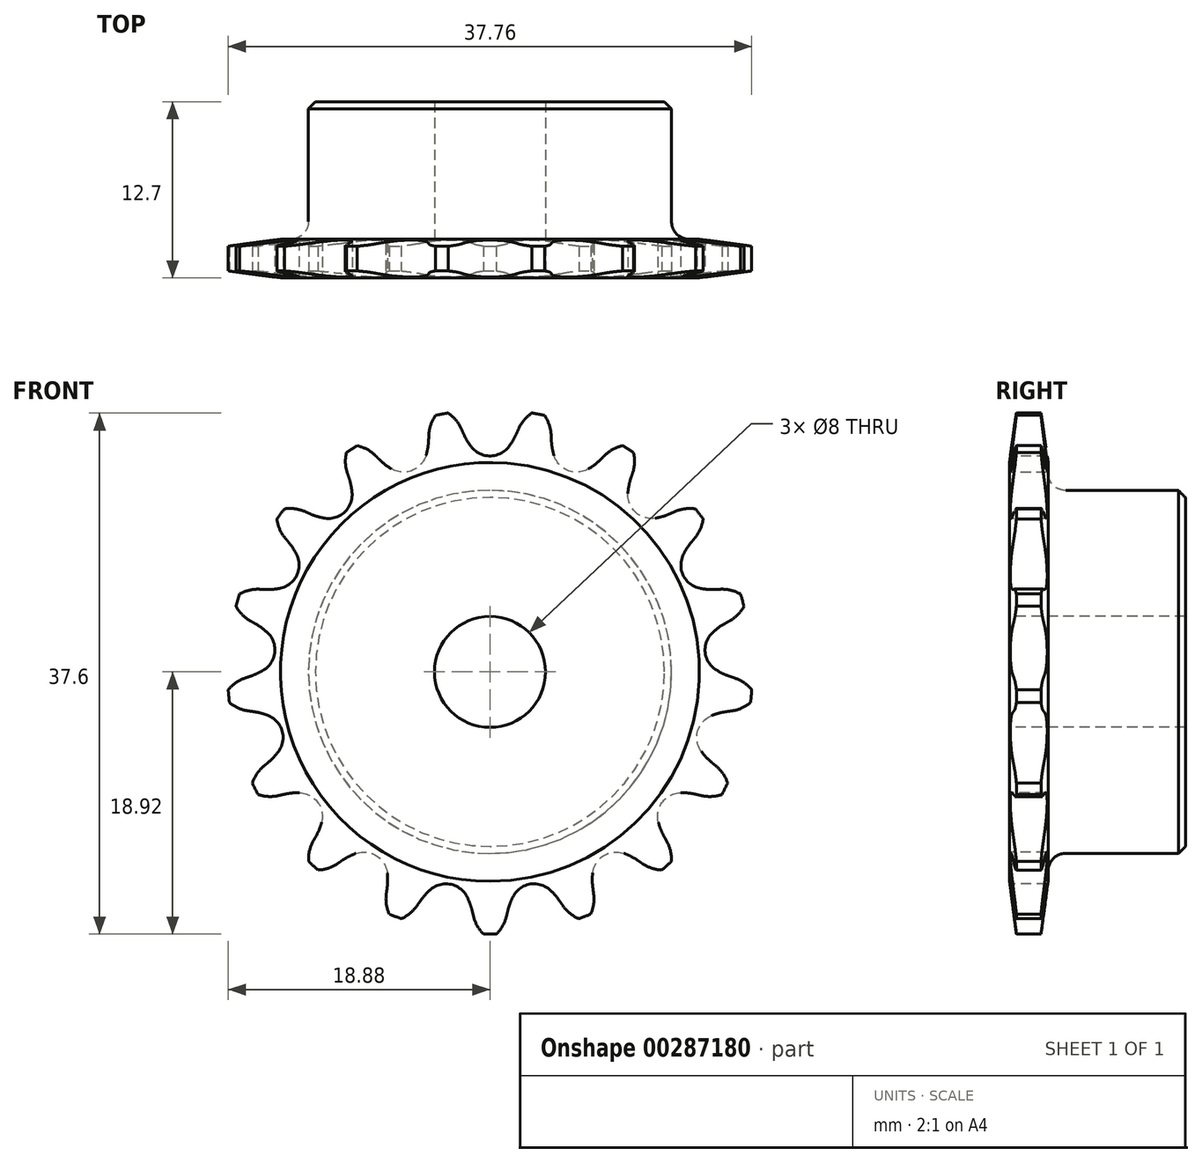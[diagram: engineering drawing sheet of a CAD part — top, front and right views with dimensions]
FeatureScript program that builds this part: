
annotation { "Feature Type Name" : "Feature", "Feature Type Description" : "" }
export const myFeature = defineFeature(function(context is Context, id is Id, definition is map)
    precondition{}
    {
        {
            var Q0;
            Q0=qCreatedBy(makeId("Right.planeOp"),FACE);
            var sketch = newSketch(context, id + "F0", { "sketchPlane" : qUnion([Q0])});
            skLineSegment(sketch, "E0", {"start": v(0, 0) * mm, "end": v(23.93, 0) * mm, "construction": true});
            skLineSegment(sketch, "E1.bottom", {"start": v(1.33, 13.1) * mm, "end": v(14.03, 13.1) * mm});
            skLineSegment(sketch, "E1.top", {"start": v(1.33, 4) * mm, "end": v(14.03, 4) * mm});
            skLineSegment(sketch, "E1.left", {"start": v(1.33, 13.1) * mm, "end": v(1.33, 4) * mm});
            skLineSegment(sketch, "E1.right", {"start": v(14.03, 13.1) * mm, "end": v(14.03, 4) * mm});
            skLineSegment(sketch, "E2.bottom", {"start": v(1.33, 4) * mm, "end": v(4.12, 4) * mm});
            skLineSegment(sketch, "E2.top", {"start": v(1.33, 18.92) * mm, "end": v(4.12, 18.92) * mm});
            skLineSegment(sketch, "E2.left", {"start": v(1.33, 4) * mm, "end": v(1.33, 18.92) * mm});
            skLineSegment(sketch, "E2.right", {"start": v(4.12, 4) * mm, "end": v(4.12, 18.92) * mm});
            skLineSegment(sketch, "E3.MirrorCS", {"start": v(1.33, -13.1) * mm, "end": v(1.33, -4) * mm});
            skLineSegment(sketch, "E4.MirrorCS", {"start": v(4.12, -4) * mm, "end": v(4.12, -18.92) * mm});
            skLineSegment(sketch, "E5.MirrorCS", {"start": v(1.33, -4) * mm, "end": v(1.33, -18.92) * mm});
            skLineSegment(sketch, "E6.MirrorCS", {"start": v(1.33, -13.1) * mm, "end": v(14.03, -13.1) * mm});
            skLineSegment(sketch, "E7.MirrorCS", {"start": v(1.33, -4) * mm, "end": v(14.03, -4) * mm});
            skLineSegment(sketch, "E8.MirrorCS", {"start": v(14.03, -13.1) * mm, "end": v(14.03, -4) * mm});
            skLineSegment(sketch, "E9.MirrorCS", {"start": v(1.33, -4) * mm, "end": v(4.12, -4) * mm});
            skLineSegment(sketch, "E10.MirrorCS", {"start": v(1.33, -18.92) * mm, "end": v(4.12, -18.92) * mm});
            skSolve(sketch);
        }
        {
            var Q0;
            {var subQ5=sQuery(id+"F0.wireOp",EDGE,"E2.top");Q0=makeQuery(id+"F0.imprint","IMPRINT",FACE,{"disambiguationData":[TD([[makeQuery(id+"F0.imprint","IMPRINT",EDGE,{"derivedFrom":subQ5}),-1.0]])]});}
            var Q1;
            {var subQ4=sQuery(id+"F0.wireOp",EDGE,"E1.top");Q1=makeQuery(id+"F0.imprint","IMPRINT",FACE,{"disambiguationData":[TD([[makeQuery(id+"F0.imprint","IMPRINT",EDGE,{"derivedFrom":subQ4}),1.0]])]});}
            var Q2;
            {var subQ0=sQuery(id+"F0.wireOp",EDGE,"E7.MirrorCS");Q2=makeQuery(id+"F0.imprint","IMPRINT",FACE,{"disambiguationData":[TD([[makeQuery(id+"F0.imprint","IMPRINT",EDGE,{"derivedFrom":subQ0}),-1.0]])]});}
            var Q3;
            {var subQ0=sQuery(id+"F0.wireOp",EDGE,"E10.MirrorCS");Q3=makeQuery(id+"F0.imprint","IMPRINT",FACE,{"disambiguationData":[TD([[makeQuery(id+"F0.imprint","IMPRINT",EDGE,{"derivedFrom":subQ0}),1.0]])]});}
            var Q4;
            {var subQ5=sQuery(id+"F0.wireOp",EDGE,"E2.bottom");Q4=makeQuery(id+"F0.imprint","IMPRINT",FACE,{"disambiguationData":[TD([[makeQuery(id+"F0.imprint","IMPRINT",EDGE,{"derivedFrom":subQ5}),1.0]])]});}
            var Q5;
            {var subQ0=sQuery(id+"F0.wireOp",EDGE,"E9.MirrorCS");Q5=makeQuery(id+"F0.imprint","IMPRINT",FACE,{"disambiguationData":[TD([[makeQuery(id+"F0.imprint","IMPRINT",EDGE,{"derivedFrom":subQ0}),-1.0]])]});}
            var Q6;
            Q6=sQuery(id+"F0.wireOp",EDGE,"E0");
            revolve(context, id + "F1", {"entities" : qUnion([Q0, Q1, Q2, Q3, Q4, Q5]), "axis" : qUnion([Q6]), "revolveType" : RevolveType.FULL});
        }
        {
            var Q0;
            Q0=makeQuery(id+"F1.opRevolve","SWEPT_EDGE",EDGE,{"disambiguationData":[OSD([sQuery(id+"F0.wireOp",EDGE,"E1.bottom"),sQuery(id+"F0.wireOp",EDGE,"E2.right")])]});
            fillet(context, id + "F2", {"entities" : qUnion([Q0]), "radius" : 1.27 * mm, "tangentPropagation" : true, "allowEdgeOverflow" : false});
        }
        {
            var Q0;
            Q0=makeQuery(id+"F1.opRevolve","SWEPT_BODY",BODY,{"disambiguationData":[OSD([sQuery(id+"F0.wireOp",EDGE,"E4.MirrorCS"),sQuery(id+"F0.wireOp",EDGE,"E5.MirrorCS"),sQuery(id+"F0.wireOp",EDGE,"E6.MirrorCS"),sQuery(id+"F0.wireOp",EDGE,"E7.MirrorCS"),sQuery(id+"F0.wireOp",EDGE,"E8.MirrorCS"),sQuery(id+"F0.wireOp",EDGE,"E9.MirrorCS"),sQuery(id+"F0.wireOp",EDGE,"E10.MirrorCS")])]});
            deleteBodies(context, id + "F3", {"entities" : qUnion([Q0])});
        }
        {
            var Q0;
            Q0=makeQuery(id+"F1.opRevolve","SWEPT_EDGE",EDGE,{"disambiguationData":[OSD([sQuery(id+"F0.wireOp",EDGE,"E1.bottom"),sQuery(id+"F0.wireOp",EDGE,"E1.right")])]});
            chamfer(context, id + "F4", {"entities" : qUnion([Q0]), "width" : 0.5 * mm, "tangentPropagation" : true});
        }
        {
            var Q0;
            Q0=makeQuery(id+"F1.opRevolve","SWEPT_EDGE",EDGE,{"disambiguationData":[OSD([sQuery(id+"F0.wireOp",EDGE,"E2.top"),sQuery(id+"F0.wireOp",EDGE,"E2.left")])]});
            var Q1;
            Q1=makeQuery(id+"F1.opRevolve","SWEPT_EDGE",EDGE,{"disambiguationData":[OSD([sQuery(id+"F0.wireOp",EDGE,"E2.top"),sQuery(id+"F0.wireOp",EDGE,"E2.right")])]});
            chamfer(context, id + "F5", {"entities" : qUnion([Q0, Q1]), "chamferType" : ChamferType.TWO_OFFSETS, "width1" : 3.8 * mm, "oppositeDirection" : false, "width2" : 0.5 * mm, "tangentPropagation" : true});
        }
        {
            var Q0;
            Q0=qCreatedBy(makeId("Front.planeOp"),FACE);
            var sketch = newSketch(context, id + "F6", { "sketchPlane" : qUnion([Q0])});
            skCircle(sketch, "E11", {"center": v(0, 0) * mm, "radius": 17.28 * mm, "construction": true});
            skLineSegment(sketch, "E12", {"start": v(0, 0) * mm, "end": v(0, 17.28) * mm, "construction": true});
            skLineSegment(sketch, "E13", {"start": v(0, 17.28) * mm, "end": v(75.89, 17.28) * mm, "construction": true});
            skLineSegment(sketch, "E14", {"start": v(0, 17.28) * mm, "end": v(2.07, 18.92) * mm, "construction": true});
            skLineSegment(sketch, "E15", {"start": v(2.07, 18.92) * mm, "end": v(-1.9, 17.17) * mm, "construction": true});
            skLineSegment(sketch, "E16", {"start": v(-1.9, 17.17) * mm, "end": v(-2.06, 17.53) * mm});
            skLineSegment(sketch, "E17", {"start": v(0, 0) * mm, "end": v(-3.54, 18.95) * mm, "construction": true});
            skArc(sketch, "E18", {"start": v(-3.54, 18.95) * mm, "mid": v(-6.56, 14.6) * mm, "end": v(-1.93, 17.17) * mm, "construction": true});
            skArc(sketch, "E19", {"start": v(-2.06, 17.53) * mm, "mid": v(-2.66, 18.39) * mm, "end": v(-3.54, 18.95) * mm});
            skArc(sketch, "E20", {"start": v(-1.9, 17.17) * mm, "mid": v(-1.65, 16.68) * mm, "end": v(-1.33, 16.22) * mm});
            skArc(sketch, "E21", {"start": v(-1.33, 16.22) * mm, "mid": v(2.68, 14.63) * mm, "end": v(6.08, 17.28) * mm, "construction": true});
            skArc(sketch, "E22.0.MirrorCS", {"start": v(1.9, 17.17) * mm, "mid": v(1.65, 16.68) * mm, "end": v(1.33, 16.22) * mm});
            skLineSegment(sketch, "E23.0.MirrorCS", {"start": v(1.9, 17.17) * mm, "end": v(2.06, 17.53) * mm});
            skArc(sketch, "E24.0.MirrorCS", {"start": v(2.06, 17.53) * mm, "mid": v(2.66, 18.39) * mm, "end": v(3.54, 18.95) * mm});
            skArc(sketch, "E25", {"start": v(-1.33, 16.22) * mm, "mid": v(0, 15.58) * mm, "end": v(1.33, 16.22) * mm});
            skArc(sketch, "E26", {"start": v(1.33, 16.22) * mm, "mid": v(0, 18.98) * mm, "end": v(-1.33, 16.22) * mm, "construction": true});
            skArc(sketch, "E27.trimOffspring", {"start": v(-1.9, 17.17) * mm, "mid": v(-1.9, 17.17) * mm, "end": v(-1.9, 17.17) * mm, "construction": true});
            skLineSegment(sketch, "E28.trimOffspring", {"start": v(3.1, 5.82) * mm, "end": v(0, 12.86) * mm, "construction": true});
            skLineSegment(sketch, "E29.1.0", {"start": v(-7.98, 15.32) * mm, "end": v(-8.25, 15.6) * mm});
            skArc(sketch, "E29.1.1", {"start": v(-8.25, 15.6) * mm, "mid": v(-9.12, 16.18) * mm, "end": v(-10.15, 16.4) * mm});
            skArc(sketch, "E29.1.2", {"start": v(-7.98, 15.32) * mm, "mid": v(-7.56, 14.96) * mm, "end": v(-7.1, 14.65) * mm});
            skArc(sketch, "E29.1.3", {"start": v(-7.1, 14.65) * mm, "mid": v(-5.63, 14.53) * mm, "end": v(-4.62, 15.6) * mm});
            skArc(sketch, "E29.1.4", {"start": v(-4.43, 16.7) * mm, "mid": v(-4.49, 16.15) * mm, "end": v(-4.62, 15.6) * mm});
            skLineSegment(sketch, "E29.1.5", {"start": v(-4.43, 16.7) * mm, "end": v(-4.41, 17.09) * mm});
            skArc(sketch, "E29.1.6", {"start": v(-4.41, 17.09) * mm, "mid": v(-4.16, 18.1) * mm, "end": v(-3.54, 18.95) * mm});
            skLineSegment(sketch, "E29.2.0", {"start": v(-12.97, 11.4) * mm, "end": v(-13.33, 11.56) * mm});
            skArc(sketch, "E29.2.1", {"start": v(-13.33, 11.56) * mm, "mid": v(-14.35, 11.8) * mm, "end": v(-15.39, 11.62) * mm});
            skArc(sketch, "E29.2.2", {"start": v(-12.97, 11.4) * mm, "mid": v(-12.45, 11.22) * mm, "end": v(-11.9, 11.1) * mm});
            skArc(sketch, "E29.2.3", {"start": v(-11.9, 11.1) * mm, "mid": v(-10.5, 11.51) * mm, "end": v(-9.95, 12.88) * mm});
            skArc(sketch, "E29.2.4", {"start": v(-10.16, 13.97) * mm, "mid": v(-10.02, 13.43) * mm, "end": v(-9.95, 12.88) * mm});
            skLineSegment(sketch, "E29.2.5", {"start": v(-10.16, 13.97) * mm, "end": v(-10.29, 14.34) * mm});
            skArc(sketch, "E29.2.6", {"start": v(-10.29, 14.34) * mm, "mid": v(-10.42, 15.38) * mm, "end": v(-10.15, 16.4) * mm});
            skLineSegment(sketch, "E29.3.0", {"start": v(-16.22, 5.95) * mm, "end": v(-16.6, 5.97) * mm});
            skArc(sketch, "E29.3.1", {"start": v(-16.6, 5.97) * mm, "mid": v(-17.65, 5.81) * mm, "end": v(-18.55, 5.28) * mm});
            skArc(sketch, "E29.3.2", {"start": v(-16.22, 5.95) * mm, "mid": v(-15.66, 5.96) * mm, "end": v(-15.11, 6.04) * mm});
            skArc(sketch, "E29.3.3", {"start": v(-15.11, 6.04) * mm, "mid": v(-13.95, 6.94) * mm, "end": v(-13.93, 8.42) * mm});
            skArc(sketch, "E29.3.4", {"start": v(-14.52, 9.36) * mm, "mid": v(-14.2, 8.9) * mm, "end": v(-13.93, 8.42) * mm});
            skLineSegment(sketch, "E29.3.5", {"start": v(-14.52, 9.36) * mm, "end": v(-14.77, 9.66) * mm});
            skArc(sketch, "E29.3.6", {"start": v(-14.77, 9.66) * mm, "mid": v(-15.27, 10.58) * mm, "end": v(-15.39, 11.62) * mm});
            skLineSegment(sketch, "E29.4.0", {"start": v(-17.27, -0.31) * mm, "end": v(-17.64, -0.43) * mm});
            skArc(sketch, "E29.4.1", {"start": v(-17.64, -0.43) * mm, "mid": v(-18.55, -0.95) * mm, "end": v(-19.2, -1.78) * mm});
            skArc(sketch, "E29.4.2", {"start": v(-17.27, -0.31) * mm, "mid": v(-16.76, -0.1) * mm, "end": v(-16.27, 0.17) * mm});
            skArc(sketch, "E29.4.3", {"start": v(-16.27, 0.17) * mm, "mid": v(-15.51, 1.44) * mm, "end": v(-16.03, 2.82) * mm});
            skArc(sketch, "E29.4.4", {"start": v(-16.92, 3.48) * mm, "mid": v(-16.45, 3.18) * mm, "end": v(-16.03, 2.82) * mm});
            skLineSegment(sketch, "E29.4.5", {"start": v(-16.92, 3.48) * mm, "end": v(-17.26, 3.67) * mm});
            skArc(sketch, "E29.4.6", {"start": v(-17.26, 3.67) * mm, "mid": v(-18.06, 4.35) * mm, "end": v(-18.55, 5.28) * mm});
            skLineSegment(sketch, "E29.5.0", {"start": v(-16, -6.53) * mm, "end": v(-16.3, -6.78) * mm});
            skArc(sketch, "E29.5.1", {"start": v(-16.3, -6.78) * mm, "mid": v(-16.96, -7.6) * mm, "end": v(-17.26, -8.6) * mm});
            skArc(sketch, "E29.5.2", {"start": v(-16, -6.53) * mm, "mid": v(-15.6, -6.15) * mm, "end": v(-15.24, -5.72) * mm});
            skArc(sketch, "E29.5.3", {"start": v(-15.24, -5.72) * mm, "mid": v(-14.99, -4.26) * mm, "end": v(-15.96, -3.16) * mm});
            skArc(sketch, "E29.5.4", {"start": v(-17.04, -2.87) * mm, "mid": v(-16.5, -2.98) * mm, "end": v(-15.96, -3.16) * mm});
            skLineSegment(sketch, "E29.5.5", {"start": v(-17.04, -2.87) * mm, "end": v(-17.42, -2.81) * mm});
            skArc(sketch, "E29.5.6", {"start": v(-17.42, -2.81) * mm, "mid": v(-18.41, -2.47) * mm, "end": v(-19.2, -1.78) * mm});
            skLineSegment(sketch, "E29.6.0", {"start": v(-12.56, -11.87) * mm, "end": v(-12.75, -12.2) * mm});
            skArc(sketch, "E29.6.1", {"start": v(-12.75, -12.2) * mm, "mid": v(-13.07, -13.2) * mm, "end": v(-13, -14.25) * mm});
            skArc(sketch, "E29.6.2", {"start": v(-12.56, -11.87) * mm, "mid": v(-12.32, -11.36) * mm, "end": v(-12.14, -10.84) * mm});
            skArc(sketch, "E29.6.3", {"start": v(-12.14, -10.84) * mm, "mid": v(-12.43, -9.39) * mm, "end": v(-13.74, -8.72) * mm});
            skArc(sketch, "E29.6.4", {"start": v(-14.85, -8.83) * mm, "mid": v(-14.3, -8.74) * mm, "end": v(-13.74, -8.72) * mm});
            skLineSegment(sketch, "E29.6.5", {"start": v(-14.85, -8.83) * mm, "end": v(-15.23, -8.92) * mm});
            skArc(sketch, "E29.6.6", {"start": v(-15.23, -8.92) * mm, "mid": v(-16.28, -8.96) * mm, "end": v(-17.26, -8.6) * mm});
            skLineSegment(sketch, "E29.7.0", {"start": v(-7.42, -15.6) * mm, "end": v(-7.47, -15.99) * mm});
            skArc(sketch, "E29.7.1", {"start": v(-7.47, -15.99) * mm, "mid": v(-7.42, -17.03) * mm, "end": v(-6.97, -17.98) * mm});
            skArc(sketch, "E29.7.2", {"start": v(-7.42, -15.6) * mm, "mid": v(-7.38, -15.05) * mm, "end": v(-7.4, -14.5) * mm});
            skArc(sketch, "E29.7.3", {"start": v(-7.4, -14.5) * mm, "mid": v(-8.2, -13.25) * mm, "end": v(-9.67, -13.1) * mm});
            skArc(sketch, "E29.7.4", {"start": v(-10.66, -13.6) * mm, "mid": v(-10.18, -13.31) * mm, "end": v(-9.67, -13.1) * mm});
            skLineSegment(sketch, "E29.7.5", {"start": v(-10.66, -13.6) * mm, "end": v(-10.98, -13.82) * mm});
            skArc(sketch, "E29.7.6", {"start": v(-10.98, -13.82) * mm, "mid": v(-11.94, -14.23) * mm, "end": v(-13, -14.25) * mm});
            skLineSegment(sketch, "E29.8.0", {"start": v(-1.28, -17.23) * mm, "end": v(-1.2, -17.6) * mm});
            skArc(sketch, "E29.8.1", {"start": v(-1.2, -17.6) * mm, "mid": v(-0.76, -18.56) * mm, "end": v(0, -19.28) * mm});
            skArc(sketch, "E29.8.2", {"start": v(-1.28, -17.23) * mm, "mid": v(-1.45, -16.7) * mm, "end": v(-1.67, -16.19) * mm});
            skArc(sketch, "E29.8.3", {"start": v(-1.67, -16.19) * mm, "mid": v(-2.86, -15.32) * mm, "end": v(-4.29, -15.7) * mm});
            skArc(sketch, "E29.8.4", {"start": v(-5.03, -16.53) * mm, "mid": v(-4.68, -16.1) * mm, "end": v(-4.29, -15.7) * mm});
            skLineSegment(sketch, "E29.8.5", {"start": v(-5.03, -16.53) * mm, "end": v(-5.25, -16.85) * mm});
            skArc(sketch, "E29.8.6", {"start": v(-5.25, -16.85) * mm, "mid": v(-6, -17.58) * mm, "end": v(-6.97, -17.98) * mm});
            skLineSegment(sketch, "E29.9.0", {"start": v(5.03, -16.53) * mm, "end": v(5.25, -16.85) * mm});
            skArc(sketch, "E29.9.1", {"start": v(5.25, -16.85) * mm, "mid": v(6, -17.58) * mm, "end": v(6.97, -17.98) * mm});
            skArc(sketch, "E29.9.2", {"start": v(5.03, -16.53) * mm, "mid": v(4.68, -16.1) * mm, "end": v(4.29, -15.7) * mm});
            skArc(sketch, "E29.9.3", {"start": v(4.29, -15.7) * mm, "mid": v(2.86, -15.32) * mm, "end": v(1.67, -16.19) * mm});
            skArc(sketch, "E29.9.4", {"start": v(1.28, -17.23) * mm, "mid": v(1.45, -16.7) * mm, "end": v(1.67, -16.19) * mm});
            skLineSegment(sketch, "E29.9.5", {"start": v(1.28, -17.23) * mm, "end": v(1.2, -17.6) * mm});
            skArc(sketch, "E29.9.6", {"start": v(1.2, -17.6) * mm, "mid": v(0.76, -18.56) * mm, "end": v(0, -19.28) * mm});
            skLineSegment(sketch, "E29.10.0", {"start": v(10.66, -13.6) * mm, "end": v(10.98, -13.82) * mm});
            skArc(sketch, "E29.10.1", {"start": v(10.98, -13.82) * mm, "mid": v(11.94, -14.23) * mm, "end": v(13, -14.25) * mm});
            skArc(sketch, "E29.10.2", {"start": v(10.66, -13.6) * mm, "mid": v(10.18, -13.31) * mm, "end": v(9.67, -13.1) * mm});
            skArc(sketch, "E29.10.3", {"start": v(9.67, -13.1) * mm, "mid": v(8.2, -13.25) * mm, "end": v(7.4, -14.5) * mm});
            skArc(sketch, "E29.10.4", {"start": v(7.42, -15.6) * mm, "mid": v(7.38, -15.05) * mm, "end": v(7.4, -14.5) * mm});
            skLineSegment(sketch, "E29.10.5", {"start": v(7.42, -15.6) * mm, "end": v(7.47, -15.99) * mm});
            skArc(sketch, "E29.10.6", {"start": v(7.47, -15.99) * mm, "mid": v(7.42, -17.03) * mm, "end": v(6.97, -17.98) * mm});
            skLineSegment(sketch, "E29.11.0", {"start": v(14.85, -8.83) * mm, "end": v(15.23, -8.92) * mm});
            skArc(sketch, "E29.11.1", {"start": v(15.23, -8.92) * mm, "mid": v(16.28, -8.96) * mm, "end": v(17.26, -8.6) * mm});
            skArc(sketch, "E29.11.2", {"start": v(14.85, -8.83) * mm, "mid": v(14.3, -8.74) * mm, "end": v(13.74, -8.72) * mm});
            skArc(sketch, "E29.11.3", {"start": v(13.74, -8.72) * mm, "mid": v(12.43, -9.39) * mm, "end": v(12.14, -10.84) * mm});
            skArc(sketch, "E29.11.4", {"start": v(12.56, -11.87) * mm, "mid": v(12.32, -11.36) * mm, "end": v(12.14, -10.84) * mm});
            skLineSegment(sketch, "E29.11.5", {"start": v(12.56, -11.87) * mm, "end": v(12.75, -12.2) * mm});
            skArc(sketch, "E29.11.6", {"start": v(12.75, -12.2) * mm, "mid": v(13.07, -13.2) * mm, "end": v(13, -14.25) * mm});
            skLineSegment(sketch, "E29.12.0", {"start": v(17.04, -2.87) * mm, "end": v(17.42, -2.81) * mm});
            skArc(sketch, "E29.12.1", {"start": v(17.42, -2.81) * mm, "mid": v(18.41, -2.47) * mm, "end": v(19.2, -1.78) * mm});
            skArc(sketch, "E29.12.2", {"start": v(17.04, -2.87) * mm, "mid": v(16.5, -2.98) * mm, "end": v(15.96, -3.16) * mm});
            skArc(sketch, "E29.12.3", {"start": v(15.96, -3.16) * mm, "mid": v(14.99, -4.26) * mm, "end": v(15.24, -5.72) * mm});
            skArc(sketch, "E29.12.4", {"start": v(16, -6.53) * mm, "mid": v(15.6, -6.15) * mm, "end": v(15.24, -5.72) * mm});
            skLineSegment(sketch, "E29.12.5", {"start": v(16, -6.53) * mm, "end": v(16.3, -6.78) * mm});
            skArc(sketch, "E29.12.6", {"start": v(16.3, -6.78) * mm, "mid": v(16.96, -7.6) * mm, "end": v(17.26, -8.6) * mm});
            skLineSegment(sketch, "E29.13.0", {"start": v(16.92, 3.48) * mm, "end": v(17.26, 3.67) * mm});
            skArc(sketch, "E29.13.1", {"start": v(17.26, 3.67) * mm, "mid": v(18.06, 4.35) * mm, "end": v(18.55, 5.28) * mm});
            skArc(sketch, "E29.13.2", {"start": v(16.92, 3.48) * mm, "mid": v(16.45, 3.18) * mm, "end": v(16.03, 2.82) * mm});
            skArc(sketch, "E29.13.3", {"start": v(16.03, 2.82) * mm, "mid": v(15.51, 1.44) * mm, "end": v(16.27, 0.17) * mm});
            skArc(sketch, "E29.13.4", {"start": v(17.27, -0.31) * mm, "mid": v(16.76, -0.1) * mm, "end": v(16.27, 0.17) * mm});
            skLineSegment(sketch, "E29.13.5", {"start": v(17.27, -0.31) * mm, "end": v(17.64, -0.43) * mm});
            skArc(sketch, "E29.13.6", {"start": v(17.64, -0.43) * mm, "mid": v(18.55, -0.95) * mm, "end": v(19.2, -1.78) * mm});
            skLineSegment(sketch, "E29.14.0", {"start": v(14.52, 9.36) * mm, "end": v(14.77, 9.66) * mm});
            skArc(sketch, "E29.14.1", {"start": v(14.77, 9.66) * mm, "mid": v(15.27, 10.58) * mm, "end": v(15.39, 11.62) * mm});
            skArc(sketch, "E29.14.2", {"start": v(14.52, 9.36) * mm, "mid": v(14.2, 8.9) * mm, "end": v(13.93, 8.42) * mm});
            skArc(sketch, "E29.14.3", {"start": v(13.93, 8.42) * mm, "mid": v(13.95, 6.94) * mm, "end": v(15.11, 6.04) * mm});
            skArc(sketch, "E29.14.4", {"start": v(16.22, 5.95) * mm, "mid": v(15.66, 5.96) * mm, "end": v(15.11, 6.04) * mm});
            skLineSegment(sketch, "E29.14.5", {"start": v(16.22, 5.95) * mm, "end": v(16.6, 5.97) * mm});
            skArc(sketch, "E29.14.6", {"start": v(16.6, 5.97) * mm, "mid": v(17.65, 5.81) * mm, "end": v(18.55, 5.28) * mm});
            skLineSegment(sketch, "E29.15.0", {"start": v(10.16, 13.97) * mm, "end": v(10.29, 14.34) * mm});
            skArc(sketch, "E29.15.1", {"start": v(10.29, 14.34) * mm, "mid": v(10.42, 15.38) * mm, "end": v(10.15, 16.4) * mm});
            skArc(sketch, "E29.15.2", {"start": v(10.16, 13.97) * mm, "mid": v(10.02, 13.43) * mm, "end": v(9.95, 12.88) * mm});
            skArc(sketch, "E29.15.3", {"start": v(9.95, 12.88) * mm, "mid": v(10.5, 11.51) * mm, "end": v(11.9, 11.1) * mm});
            skArc(sketch, "E29.15.4", {"start": v(12.97, 11.4) * mm, "mid": v(12.45, 11.22) * mm, "end": v(11.9, 11.1) * mm});
            skLineSegment(sketch, "E29.15.5", {"start": v(12.97, 11.4) * mm, "end": v(13.33, 11.56) * mm});
            skArc(sketch, "E29.15.6", {"start": v(13.33, 11.56) * mm, "mid": v(14.35, 11.8) * mm, "end": v(15.39, 11.62) * mm});
            skLineSegment(sketch, "E29.16.0", {"start": v(4.43, 16.7) * mm, "end": v(4.41, 17.09) * mm});
            skArc(sketch, "E29.16.1", {"start": v(4.41, 17.09) * mm, "mid": v(4.16, 18.1) * mm, "end": v(3.54, 18.95) * mm});
            skArc(sketch, "E29.16.2", {"start": v(4.43, 16.7) * mm, "mid": v(4.49, 16.15) * mm, "end": v(4.62, 15.6) * mm});
            skArc(sketch, "E29.16.3", {"start": v(4.62, 15.6) * mm, "mid": v(5.63, 14.53) * mm, "end": v(7.1, 14.65) * mm});
            skArc(sketch, "E29.16.4", {"start": v(7.98, 15.32) * mm, "mid": v(7.56, 14.96) * mm, "end": v(7.1, 14.65) * mm});
            skLineSegment(sketch, "E29.16.5", {"start": v(7.98, 15.32) * mm, "end": v(8.25, 15.6) * mm});
            skArc(sketch, "E29.16.6", {"start": v(8.25, 15.6) * mm, "mid": v(9.12, 16.18) * mm, "end": v(10.15, 16.4) * mm});
            skSolve(sketch);
        }
        {
            var Q0;
            Q0 = qSketchRegion(id + "F6", true);
            extrude(context, id + "F7", {"entities" : qUnion([Q0]), "operationType" : NewBodyOperationType.INTERSECT, "oppositeDirection" : true, "depth" : 25.4 * mm});
        }
    });
